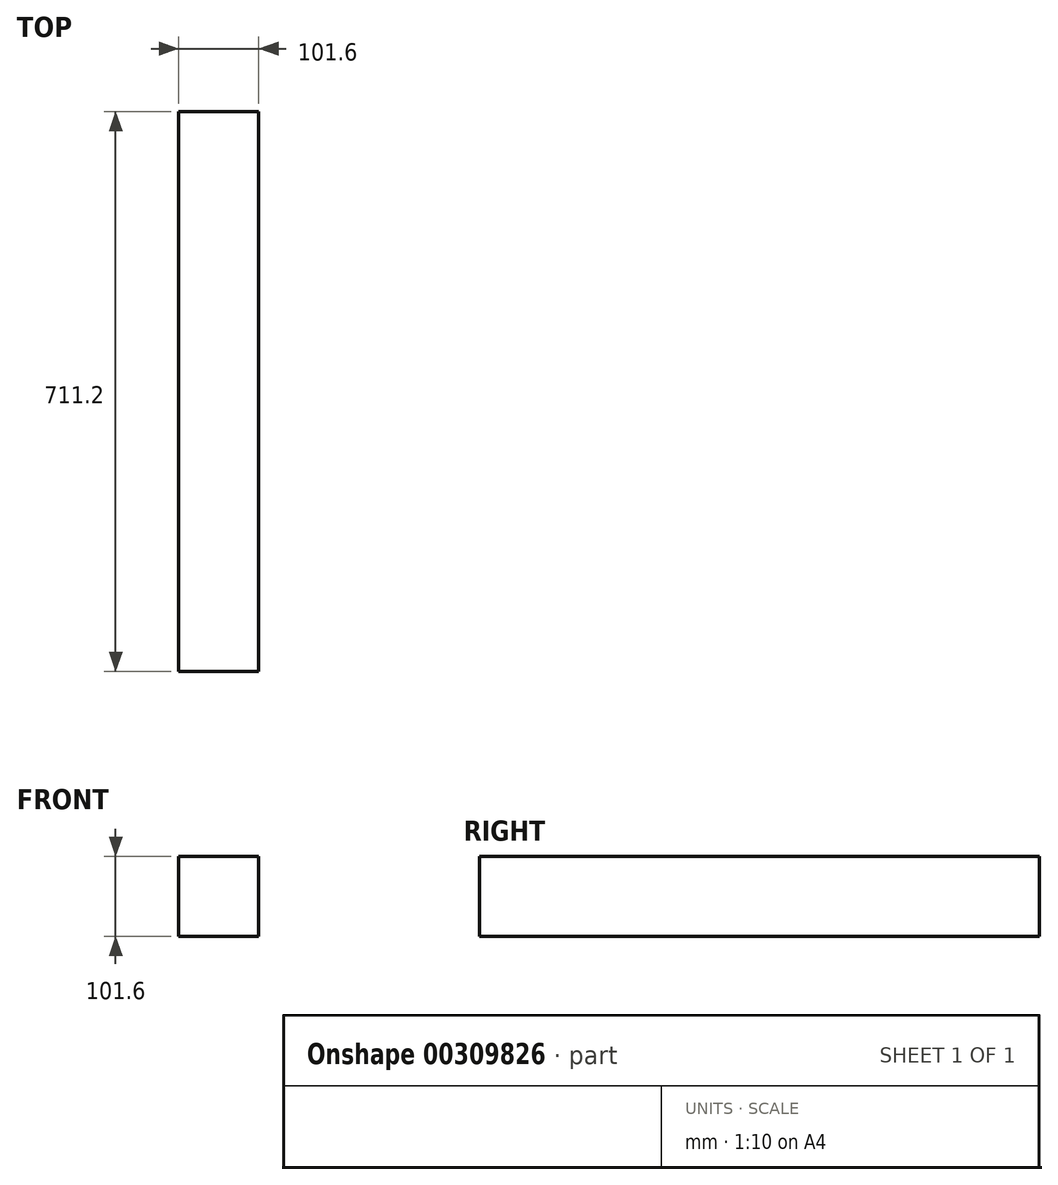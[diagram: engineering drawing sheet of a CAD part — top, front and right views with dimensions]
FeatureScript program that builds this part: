
annotation { "Feature Type Name" : "Feature", "Feature Type Description" : "" }
export const myFeature = defineFeature(function(context is Context, id is Id, definition is map)
    precondition{}
    {
        {
            var Q0;
            Q0=qCreatedBy(makeId("Front.planeOp"),FACE);
            var sketch = newSketch(context, id + "F0", { "sketchPlane" : qUnion([Q0])});
            skLineSegment(sketch, "E0.bottom", {"start": v(50.8, 50.8) * mm, "end": v(-50.8, 50.8) * mm});
            skLineSegment(sketch, "E0.top", {"start": v(50.8, -50.8) * mm, "end": v(-50.8, -50.8) * mm});
            skLineSegment(sketch, "E0.left", {"start": v(50.8, 50.8) * mm, "end": v(50.8, -50.8) * mm});
            skLineSegment(sketch, "E0.right", {"start": v(-50.8, 50.8) * mm, "end": v(-50.8, -50.8) * mm});
            skPoint(sketch, "E0.middle", {"position": v(0, 0) * mm});
            skSolve(sketch);
        }
        {
            var Q0;
            Q0 = qSketchRegion(id + "F0", true);
            extrude(context, id + "F1", {"entities" : qUnion([Q0]), "depth" : 711.2 * mm});
        }
    });
